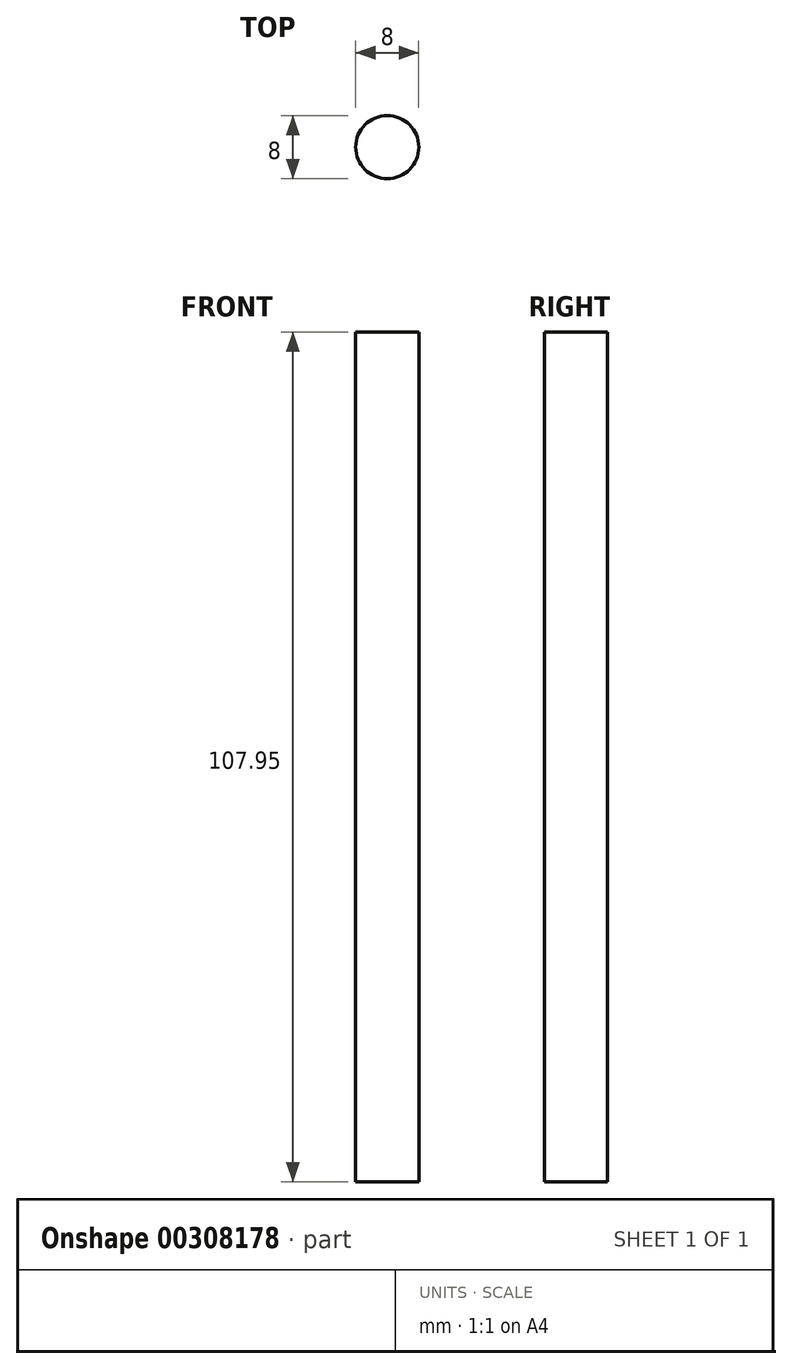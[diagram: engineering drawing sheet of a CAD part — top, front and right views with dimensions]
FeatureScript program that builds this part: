
annotation { "Feature Type Name" : "Feature", "Feature Type Description" : "" }
export const myFeature = defineFeature(function(context is Context, id is Id, definition is map)
    precondition{}
    {
        {
            var Q0;
            Q0=qCreatedBy(makeId("Top.planeOp"),FACE);
            var sketch = newSketch(context, id + "F0", { "sketchPlane" : qUnion([Q0])});
            skCircle(sketch, "E0", {"center": v(0, 0) * mm, "radius": 4 * mm});
            skSolve(sketch);
        }
        {
            var Q0;
            Q0=makeQuery(id+"F0.imprint","IMPRINT",FACE,{"disambiguationData":[TD([[makeQuery(id+"F0.imprint","IMPRINT",EDGE,{"derivedFrom":sQuery(id+"F0.wireOp",EDGE,"E0")}),1.0]])]});
            extrude(context, id + "F1", {"entities" : qUnion([Q0]), "depth" : 107.95 * mm});
        }
    });
